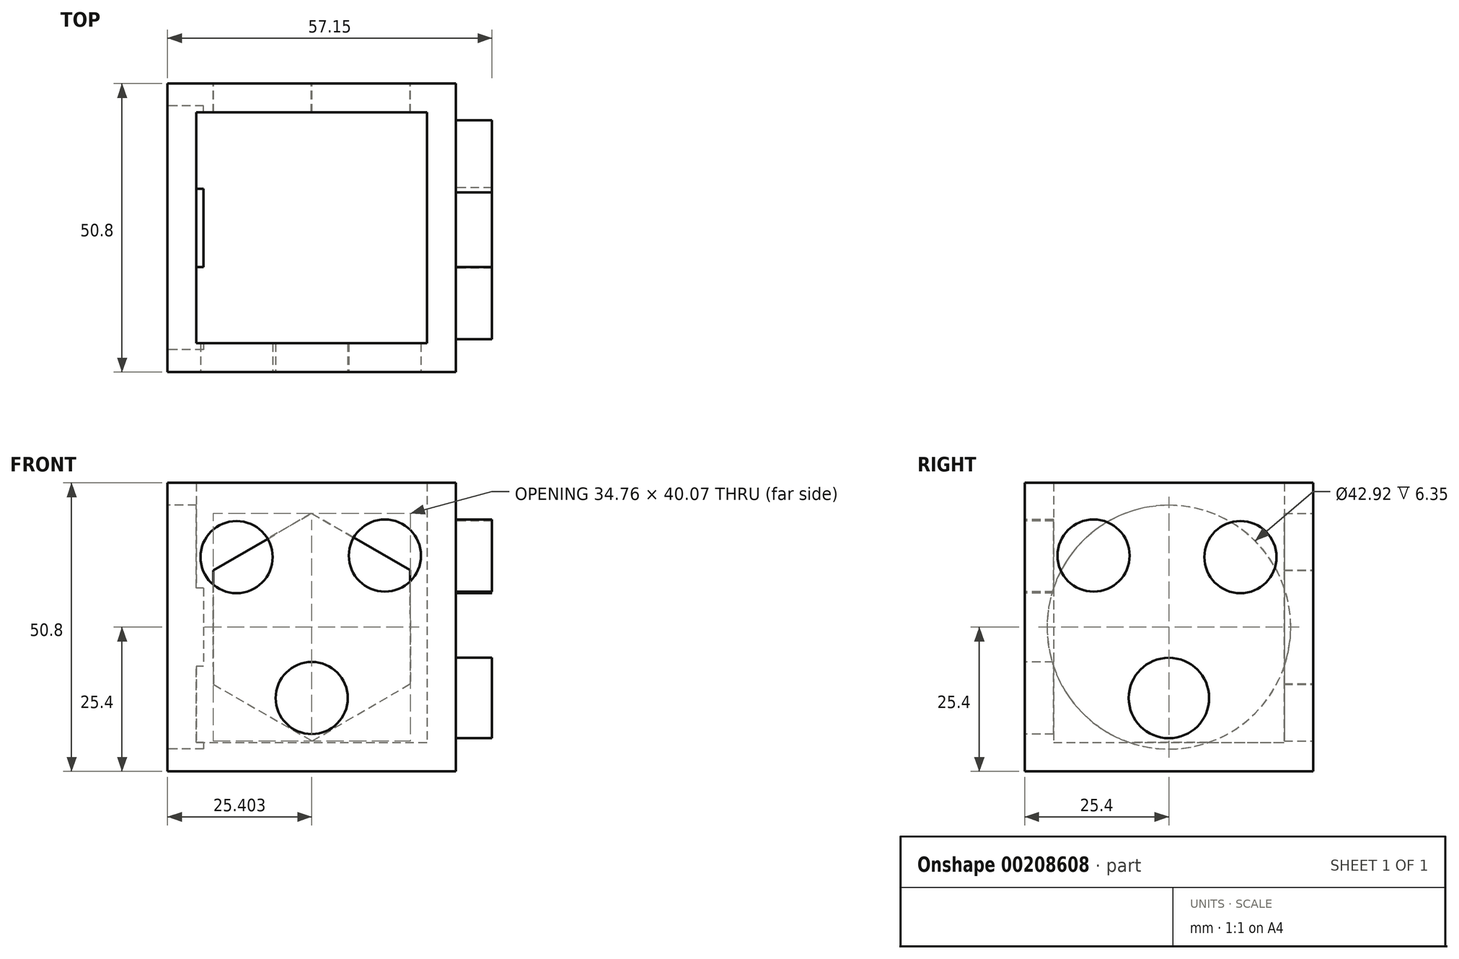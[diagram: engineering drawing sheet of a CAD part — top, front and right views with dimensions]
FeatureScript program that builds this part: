
annotation { "Feature Type Name" : "Feature", "Feature Type Description" : "" }
export const myFeature = defineFeature(function(context is Context, id is Id, definition is map)
    precondition{}
    {
        {
            var Q0;
            Q0=qCreatedBy(makeId("Front.planeOp"),FACE);
            var sketch = newSketch(context, id + "F0", { "sketchPlane" : qUnion([Q0])});
            skLineSegment(sketch, "E0.bottom", {"start": v(-57.22, 0) * mm, "end": v(-6.42, 0) * mm});
            skLineSegment(sketch, "E0.top", {"start": v(-57.22, -50.8) * mm, "end": v(-6.42, -50.8) * mm});
            skLineSegment(sketch, "E0.left", {"start": v(-57.22, 0) * mm, "end": v(-57.22, -50.8) * mm});
            skLineSegment(sketch, "E0.right", {"start": v(-6.42, 0) * mm, "end": v(-6.42, -50.8) * mm});
            skSolve(sketch);
        }
        {
            var Q0;
            Q0 = qSketchRegion(id + "F0", true);
            extrude(context, id + "F1", {"entities" : qUnion([Q0]), "depth" : 50.8 * mm});
        }
        {
            var Q0;
            Q0=makeQuery(id+"F1.opExtrude","SWEPT_FACE",FACE,{"disambiguationData":[OSD([sQuery(id+"F0.wireOp",EDGE,"E0.bottom")])]});
            var sketch = newSketch(context, id + "F2", { "sketchPlane" : qUnion([Q0])});
            skLineSegment(sketch, "E1", {"start": v(-31.82, 0) * mm, "end": v(-31.82, -50.8) * mm, "construction": true});
            skLineSegment(sketch, "E2", {"start": v(-57.22, -25.4) * mm, "end": v(-6.42, -25.4) * mm, "construction": true});
            skSolve(sketch);
        }
        {
            var Q0;
            Q0=makeQuery(id+"F1.opExtrude","SWEPT_FACE",FACE,{"disambiguationData":[OSD([sQuery(id+"F0.wireOp",EDGE,"E0.bottom")])]});
            shell(context, id + "F3", {"entities" : qUnion([Q0]), "thickness" : 5.08 * mm});
        }
        {
            var Q0;
            Q0=makeQuery(id+"F1.opExtrude","CAP_FACE",FACE,{"disambiguationData":[OSD([sQuery(id+"F0.wireOp",EDGE,"E0.bottom"),sQuery(id+"F0.wireOp",EDGE,"E0.top"),sQuery(id+"F0.wireOp",EDGE,"E0.left"),sQuery(id+"F0.wireOp",EDGE,"E0.right")])],"isStart":true});
            var sketch = newSketch(context, id + "F4", { "sketchPlane" : qUnion([Q0])});
            skLineSegment(sketch, "E3", {"start": v(31.82, 0) * mm, "end": v(31.82, -50.8) * mm, "construction": true});
            skLineSegment(sketch, "E4", {"start": v(6.42, -25.4) * mm, "end": v(57.22, -25.4) * mm, "construction": true});
            skCircle(sketch, "E5.cCircle", {"center": v(31.82, -25.4) * mm, "radius": 17.35 * mm, "construction": true});
            skLineSegment(sketch, "E5.0", {"start": v(31.88, -5.37) * mm, "end": v(49.2, -15.44) * mm});
            skLineSegment(sketch, "E5.1", {"start": v(49.2, -15.44) * mm, "end": v(49.14, -35.47) * mm});
            skLineSegment(sketch, "E5.2", {"start": v(49.14, -35.47) * mm, "end": v(31.75, -45.43) * mm});
            skLineSegment(sketch, "E5.3", {"start": v(31.75, -45.43) * mm, "end": v(14.44, -35.36) * mm});
            skLineSegment(sketch, "E5.4", {"start": v(14.44, -35.36) * mm, "end": v(14.5, -15.33) * mm});
            skLineSegment(sketch, "E5.5", {"start": v(14.5, -15.33) * mm, "end": v(31.88, -5.37) * mm});
            skPoint(sketch, "E5.0.midPoint", {"position": v(40.54, -10.4) * mm});
            skSolve(sketch);
        }
        {
            var Q0;
            Q0=makeQuery(id+"F4.imprint","IMPRINT",FACE,{"disambiguationData":[TD([[makeQuery(id+"F4.imprint","IMPRINT",EDGE,{"derivedFrom":sQuery(id+"F4.wireOp",EDGE,"E5.0")}),-1.0]])]});
            extrude(context, id + "F5", {"entities" : qUnion([Q0]), "operationType" : NewBodyOperationType.REMOVE, "oppositeDirection" : true, "depth" : 6.35 * mm});
        }
        {
            var Q0;
            Q0=makeQuery(id+"F1.opExtrude","SWEPT_FACE",FACE,{"disambiguationData":[OSD([sQuery(id+"F0.wireOp",EDGE,"E0.left")])]});
            var sketch = newSketch(context, id + "F6", { "sketchPlane" : qUnion([Q0])});
            skLineSegment(sketch, "E6", {"start": v(25.4, 0) * mm, "end": v(25.4, -50.8) * mm, "construction": true});
            skLineSegment(sketch, "E7", {"start": v(0, -25.4) * mm, "end": v(50.8, -25.4) * mm, "construction": true});
            skCircle(sketch, "E8", {"center": v(25.4, -25.4) * mm, "radius": 21.46 * mm});
            skSolve(sketch);
        }
        {
            var Q0;
            Q0 = qSketchRegion(id + "F6", true);
            extrude(context, id + "F7", {"entities" : qUnion([Q0]), "operationType" : NewBodyOperationType.REMOVE, "oppositeDirection" : true, "depth" : 6.35 * mm});
        }
        {
            var Q0;
            Q0=makeQuery(id+"F1.opExtrude","SWEPT_FACE",FACE,{"disambiguationData":[OSD([sQuery(id+"F0.wireOp",EDGE,"E0.right")])]});
            var sketch = newSketch(context, id + "F8", { "sketchPlane" : qUnion([Q0])});
            skLineSegment(sketch, "E9", {"start": v(-25.4, 0) * mm, "end": v(-25.4, -50.8) * mm, "construction": true});
            skLineSegment(sketch, "E10", {"start": v(-50.8, -25.4) * mm, "end": v(0, -25.4) * mm, "construction": true});
            skCircle(sketch, "E11", {"center": v(-38.67, -12.8) * mm, "radius": 6.35 * mm});
            skCircle(sketch, "E12", {"center": v(-12.8, -13.07) * mm, "radius": 6.35 * mm});
            skCircle(sketch, "E13", {"center": v(-25.4, -37.87) * mm, "radius": 7.08 * mm});
            skSolve(sketch);
        }
        {
            var Q0;
            Q0 = qSketchRegion(id + "F8", true);
            extrude(context, id + "F9", {"entities" : qUnion([Q0]), "operationType" : NewBodyOperationType.ADD, "depth" : 6.35 * mm});
        }
        {
            var Q0;
            Q0=makeQuery(id+"F1.opExtrude","CAP_FACE",FACE,{"disambiguationData":[OSD([sQuery(id+"F0.wireOp",EDGE,"E0.bottom"),sQuery(id+"F0.wireOp",EDGE,"E0.top"),sQuery(id+"F0.wireOp",EDGE,"E0.left"),sQuery(id+"F0.wireOp",EDGE,"E0.right")])],"isStart":false});
            var sketch = newSketch(context, id + "F10", { "sketchPlane" : qUnion([Q0])});
            skLineSegment(sketch, "E14", {"start": v(-31.82, 0) * mm, "end": v(-31.82, -50.8) * mm, "construction": true});
            skLineSegment(sketch, "E15", {"start": v(-57.22, -25.4) * mm, "end": v(-6.42, -25.4) * mm, "construction": true});
            skCircle(sketch, "E16", {"center": v(-31.82, -37.87) * mm, "radius": 6.35 * mm});
            skCircle(sketch, "E17", {"center": v(-18.94, -12.8) * mm, "radius": 6.35 * mm});
            skCircle(sketch, "E18", {"center": v(-45.07, -13.07) * mm, "radius": 6.35 * mm});
            skSolve(sketch);
        }
        {
            var Q0;
            Q0 = qSketchRegion(id + "F10", true);
            extrude(context, id + "F11", {"entities" : qUnion([Q0]), "operationType" : NewBodyOperationType.REMOVE, "oppositeDirection" : true, "depth" : 6.35 * mm});
        }
    });
